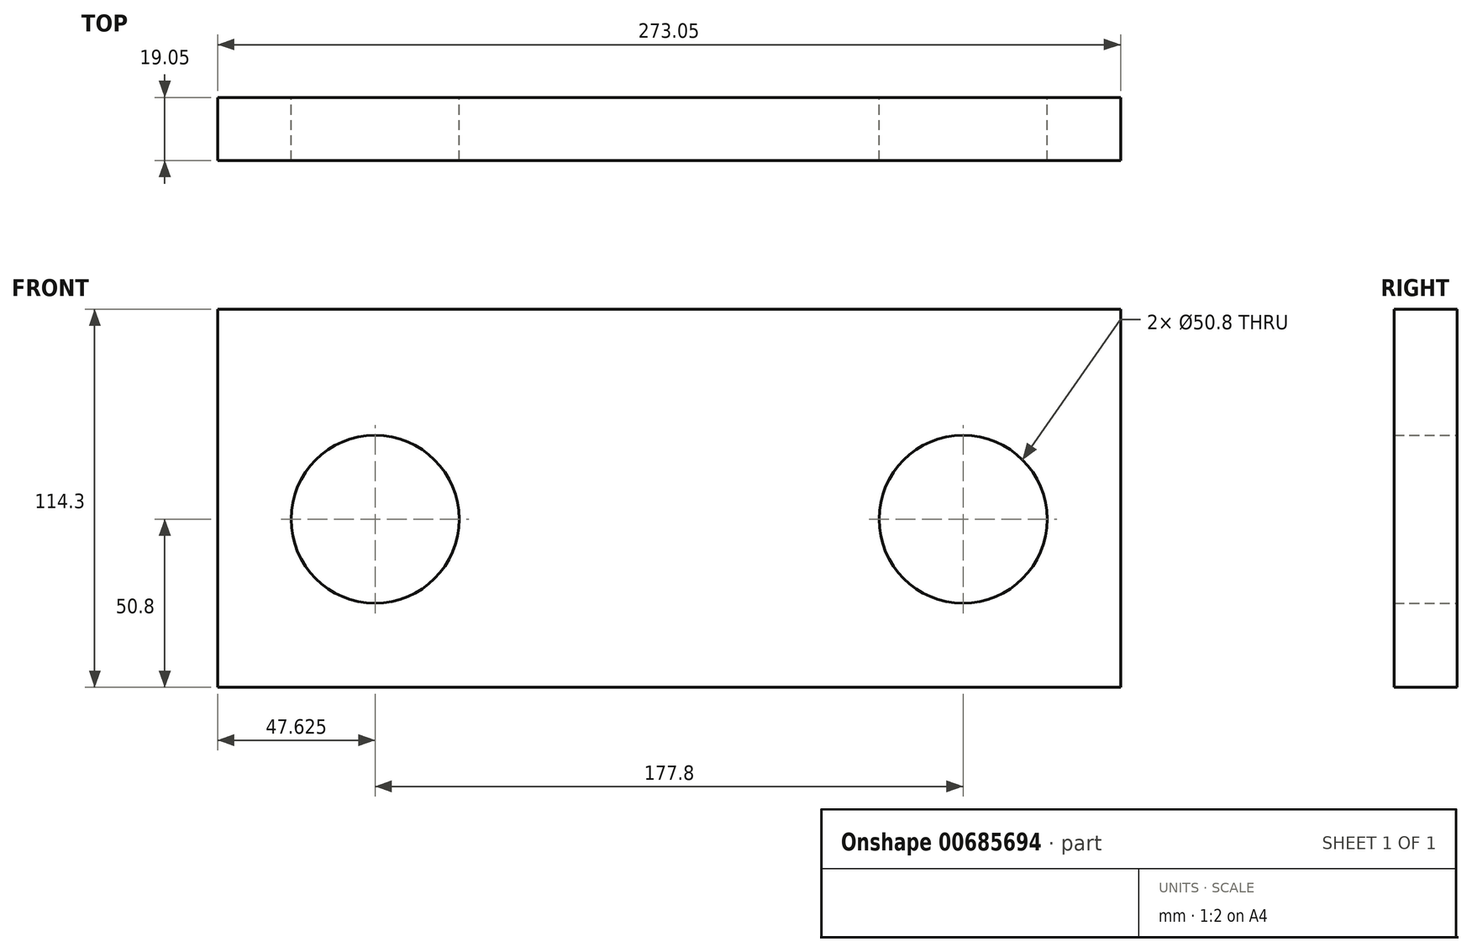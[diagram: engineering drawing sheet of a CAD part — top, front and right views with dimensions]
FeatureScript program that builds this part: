
annotation { "Feature Type Name" : "Feature", "Feature Type Description" : "" }
export const myFeature = defineFeature(function(context is Context, id is Id, definition is map)
    precondition{}
    {
        {
            var Q0;
            Q0=qCreatedBy(makeId("Front.planeOp"),FACE);
            var sketch = newSketch(context, id + "F0", { "sketchPlane" : qUnion([Q0])});
            skLineSegment(sketch, "E0.bottom", {"start": v(0, 0) * mm, "end": v(273.05, 0) * mm});
            skLineSegment(sketch, "E0.top", {"start": v(0, 114.3) * mm, "end": v(273.05, 114.3) * mm});
            skLineSegment(sketch, "E0.left", {"start": v(0, 0) * mm, "end": v(0, 114.3) * mm});
            skLineSegment(sketch, "E0.right", {"start": v(273.05, 0) * mm, "end": v(273.05, 114.3) * mm});
            skSolve(sketch);
        }
        {
            var Q0;
            Q0=makeQuery(id+"F0.imprint","IMPRINT",FACE,{"disambiguationData":[TD([[makeQuery(id+"F0.imprint","IMPRINT",EDGE,{"derivedFrom":sQuery(id+"F0.wireOp",EDGE,"E0.bottom")}),1.0]])]});
            var sketch = newSketch(context, id + "F1", { "sketchPlane" : qUnion([Q0])});
            skCircle(sketch, "E1", {"center": v(47.63, 50.8) * mm, "radius": 25.4 * mm});
            skCircle(sketch, "E2", {"center": v(225.43, 50.8) * mm, "radius": 25.4 * mm});
            skSolve(sketch);
        }
        {
            var Q0;
            Q0=makeQuery(id+"F1.imprint","IMPRINT",FACE,{"disambiguationData":[TD([[makeQuery(id+"F1.imprint","IMPRINT",EDGE,{"derivedFrom":sQuery(id+"F1.wireOp",EDGE,"E1")}),-1.0]])]});
            extrude(context, id + "F2", {"entities" : qUnion([Q0]), "depth" : 19.05 * mm, "offsetDistance" : 25.4 * mm});
        }
        {
            var Q0;
            Q0=qSketchRegion(id+"F1",true);
            extrude(context, id + "F3", {"entities" : qUnion([Q0]), "operationType" : NewBodyOperationType.REMOVE, "oppositeDirection" : true, "depth" : 25.4 * mm, "offsetDistance" : 25.4 * mm});
        }
    });
